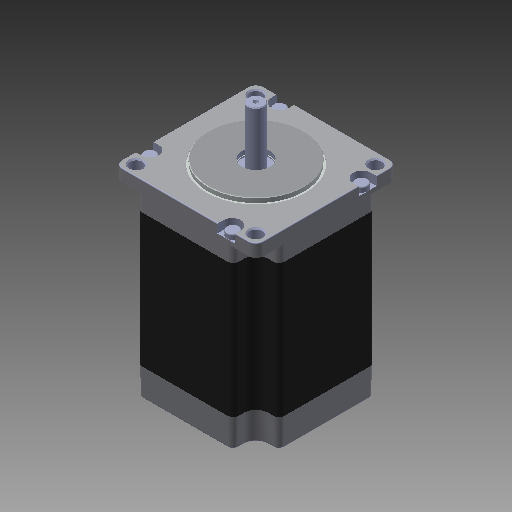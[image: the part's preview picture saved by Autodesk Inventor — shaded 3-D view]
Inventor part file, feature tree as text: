
AUTODESK INVENTOR PART (.ipt)
format: ipt  version: 2018 (Build 220112000, 112)  size: 424,448 bytes
history: native  units: in
note: dims shown in document units (in); Inventor stores cm internally (conversion verified against a paired STEP export)
features: other x3, imported_body x2, extrude x1, sketch x1
ambient origin geometry x8: Origin, YZ Plane, XZ Plane, XY Plane, X Axis, Y Axis, Z Axis, Center Point
bodies: Body1 (feature_tree), Body2 (feature_tree), Body3 (feature_tree), Body4 (feature_tree)
feature tree (7):
  other  "Фаска2"
  other  "stepper motor NEMA 23 57x761"
  extrude  "Extrusion1"  [1 undecoded]
  other  "Вырез-Вытянуть12"
  imported_body  "Base1"
  imported_body  "Base2"
  sketch  "Sketch1"  dims[d0=0.5906in d1=0.0in]
note: 1 required parameter value undecoded (feature->parameter linkage not recoverable at this tier; creation-order binding heuristic only, values carry confidence <= 0.55)
